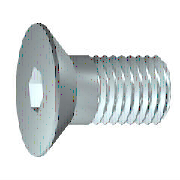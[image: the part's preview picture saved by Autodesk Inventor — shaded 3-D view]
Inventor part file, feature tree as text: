
AUTODESK INVENTOR PART (.ipt)
format: ipt  version: 2021.4 (Build 254397000, 397)  size: 195,584 bytes
history: native  units: mm (DEFAULTED — no unit token found)
features: other x4, sketch x3, fillet x1, chamfer x1
ambient origin geometry x8: Origin, YZ Plane, XZ Plane, XY Plane, X Axis, Y Axis, Z Axis, Center Point
bodies: Solid1 (feature_tree)
feature tree (9):
  sketch  "Sketch1"  dims[d2=3.0mm]
  other  "WorkPoint1"
  sketch  "Sketch2"  dims[d3=6.0mm]
  fillet  "Fillet1"  [1 undecoded]
  chamfer  "Chamfer1"  Distance=3.0mm
  other  "MSC_A1"
  other  "MSC_PF1"
  other  "MSC_PT1"
  sketch  "Sketch3"  dims[d4=1.5mm d5=3.0mm d6=8.0mm d7=10.0mm d8=360.0deg d9=0.0mm d10=2.0mm d11=4.0mm d12=120.0deg d13=120.0deg d14=120.0deg d15=120.0deg d16=2.5mm d17=0.0mm d18=0.3mm d19=0.5mm d20=45.0deg d22=0.0mm d23=0.0mm d35=0.0mm d37=0.0mm d38=0.0mm d39=0.5mm d40=0.0mm d41=0.0mm d42=0.0mm d43=45.0deg]
note: 1 required parameter value undecoded (feature->parameter linkage not recoverable at this tier; creation-order binding heuristic only, values carry confidence <= 0.55)
